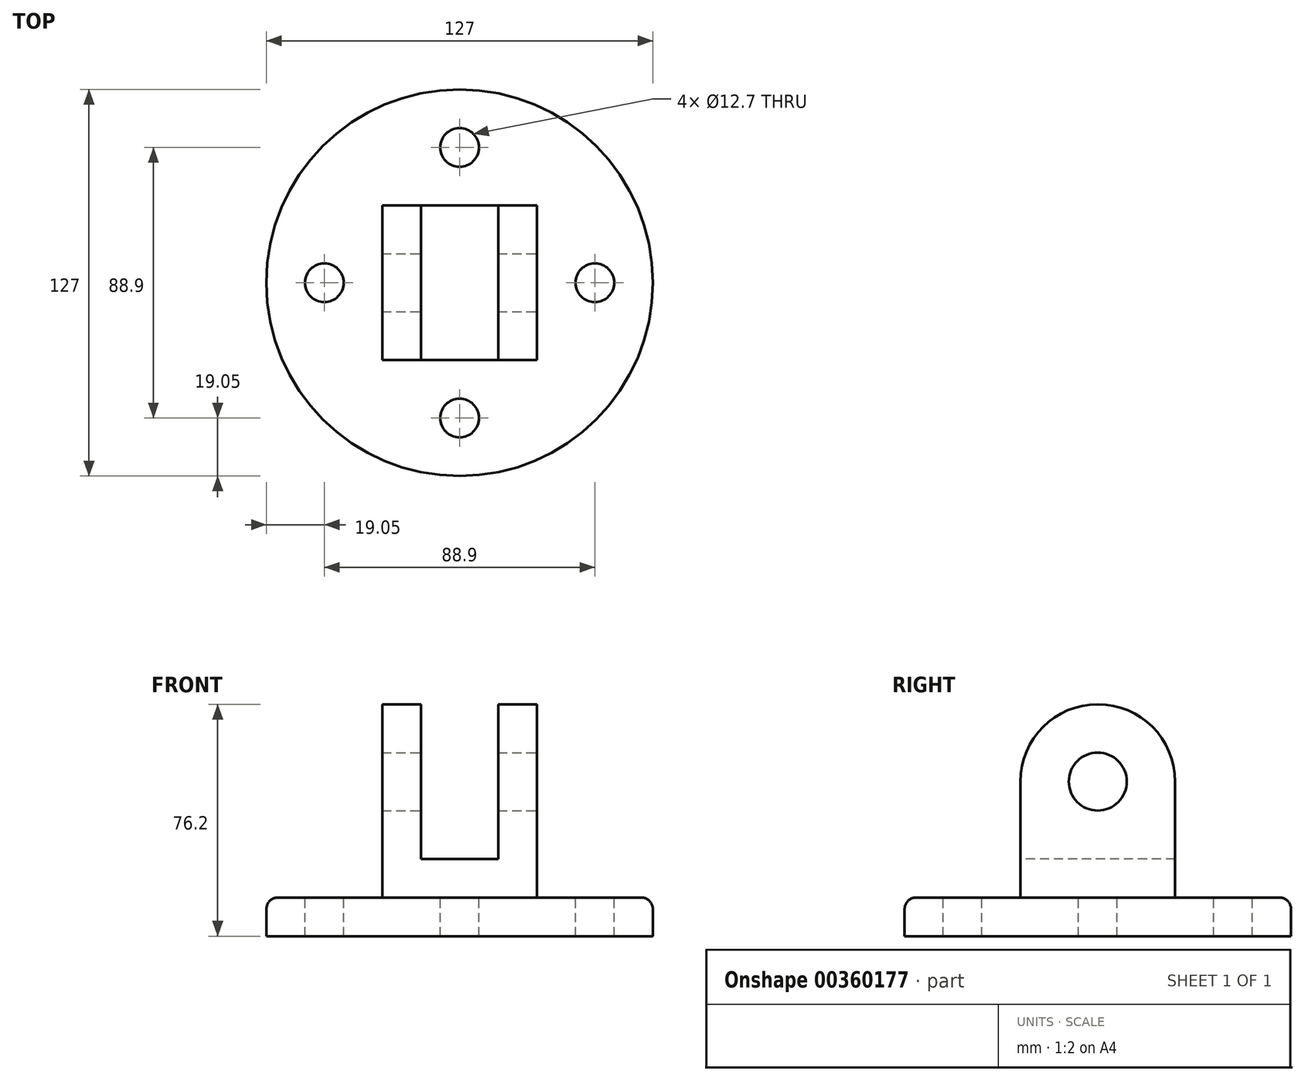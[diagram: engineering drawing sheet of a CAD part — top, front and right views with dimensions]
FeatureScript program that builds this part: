
annotation { "Feature Type Name" : "Feature", "Feature Type Description" : "" }
export const myFeature = defineFeature(function(context is Context, id is Id, definition is map)
    precondition{}
    {
        {
            var Q0;
            Q0=qCreatedBy(makeId("Top.planeOp"),FACE);
            var sketch = newSketch(context, id + "F0", { "sketchPlane" : qUnion([Q0])});
            skCircle(sketch, "E0", {"center": v(0, 0) * mm, "radius": 63.5 * mm});
            skSolve(sketch);
        }
        {
            var Q0;
            Q0=makeQuery(id+"F0.imprint","IMPRINT",FACE,{"disambiguationData":[TD([[makeQuery(id+"F0.imprint","IMPRINT",EDGE,{"derivedFrom":sQuery(id+"F0.wireOp",EDGE,"E0")}),1.0]])]});
            extrude(context, id + "F1", {"entities" : qUnion([Q0]), "depth" : 12.7 * mm});
        }
        {
            var Q0;
            Q0=makeQuery(id+"F1.opExtrude","CAP_FACE",FACE,{"disambiguationData":[OSD([sQuery(id+"F0.wireOp",EDGE,"E0")])],"isStart":false});
            var sketch = newSketch(context, id + "F2", { "sketchPlane" : qUnion([Q0])});
            skCircle(sketch, "E1", {"center": v(0, 0) * mm, "radius": 44.45 * mm, "construction": true});
            skPoint(sketch, "E2", {"position": v(0, 44.45) * mm});
            skPoint(sketch, "E3", {"position": v(-44.45, 0) * mm});
            skPoint(sketch, "E4", {"position": v(0, -44.45) * mm});
            skPoint(sketch, "E5", {"position": v(44.45, 0) * mm});
            skSolve(sketch);
        }
        {
            var Q0;
            Q0=sQuery(id+"F2.wireOp",VERTEX,"E2");
            var Q1;
            Q1=sQuery(id+"F2.wireOp",VERTEX,"E3");
            var Q2;
            Q2=sQuery(id+"F2.wireOp",VERTEX,"E4");
            var Q3;
            Q3=sQuery(id+"F2.wireOp",VERTEX,"E5");
            var Q4;
            Q4=makeQuery(id+"F1.opExtrude","SWEPT_BODY",BODY,{"disambiguationData":[OSD([sQuery(id+"F0.wireOp",EDGE,"E0")])]});
            hole(context, id + "F3", {"style" : HoleStyle.SIMPLE, "endStyle" : HoleEndStyle.THROUGH, "holeDiameter" : 12.7 * mm, "isTappedThrough" : true, "tappedDepth" : 12.7 * mm, "tapClearance" : 3, "locations" : qUnion([Q0, Q1, Q2, Q3]), "scope" : qUnion([Q4])});
        }
        {
            var Q0;
            Q0=qCreatedBy(makeId("Front.planeOp"),FACE);
            var sketch = newSketch(context, id + "F4", { "sketchPlane" : qUnion([Q0])});
            skLineSegment(sketch, "E6.top", {"start": v(-25.4, 50.8) * mm, "end": v(25.4, 50.8) * mm});
            skLineSegment(sketch, "E6.left", {"start": v(-25.4, 12.7) * mm, "end": v(-25.4, 50.8) * mm});
            skLineSegment(sketch, "E6.right", {"start": v(25.4, 12.7) * mm, "end": v(25.4, 50.8) * mm});
            skLineSegment(sketch, "E7", {"start": v(25.4, 12.7) * mm, "end": v(-25.4, 12.7) * mm});
            skSolve(sketch);
        }
        {
            var Q0;
            Q0=makeQuery(id+"F4.imprint","IMPRINT",FACE,{"disambiguationData":[TD([[makeQuery(id+"F4.imprint","IMPRINT",EDGE,{"derivedFrom":sQuery(id+"F4.wireOp",EDGE,"E6.top")}),-1.0]])]});
            extrude(context, id + "F5", {"entities" : qUnion([Q0]), "operationType" : NewBodyOperationType.ADD, "endBound" : BoundingType.SYMMETRIC, "depth" : 50.8 * mm});
        }
        {
            var Q0;
            Q0=makeQuery(id+"F5.opExtrude","CAP_FACE",FACE,{"disambiguationData":[OSD([sQuery(id+"F4.wireOp",EDGE,"E6.top"),sQuery(id+"F4.wireOp",EDGE,"E6.left"),sQuery(id+"F4.wireOp",EDGE,"E6.right"),sQuery(id+"F4.wireOp",EDGE,"E7")])],"isStart":false});
            var sketch = newSketch(context, id + "F6", { "sketchPlane" : qUnion([Q0])});
            skLineSegment(sketch, "E8.bottom", {"start": v(-12.7, 50.8) * mm, "end": v(12.7, 50.8) * mm});
            skLineSegment(sketch, "E8.top", {"start": v(-12.7, 25.4) * mm, "end": v(12.7, 25.4) * mm});
            skLineSegment(sketch, "E8.left", {"start": v(-12.7, 50.8) * mm, "end": v(-12.7, 25.4) * mm});
            skLineSegment(sketch, "E8.right", {"start": v(12.7, 50.8) * mm, "end": v(12.7, 25.4) * mm});
            skSolve(sketch);
        }
        {
            var Q0;
            Q0=makeQuery(id+"F6.imprint","IMPRINT",FACE,{"disambiguationData":[TD([[makeQuery(id+"F6.imprint","IMPRINT",EDGE,{"derivedFrom":sQuery(id+"F6.wireOp",EDGE,"E8.bottom")}),-1.0]])]});
            extrude(context, id + "F7", {"entities" : qUnion([Q0]), "operationType" : NewBodyOperationType.REMOVE, "endBound" : BoundingType.THROUGH_ALL, "oppositeDirection" : true, "depth" : 25.4 * mm});
        }
        {
            var Q0;
            Q0=makeQuery(id+"F1.opExtrude","CAP_EDGE",EDGE,{"disambiguationData":[OSD([sQuery(id+"F0.wireOp",EDGE,"E0")])],"isStart":false});
            var Q1;
            Q1=makeQuery(id+"F5.opExtrude","CAP_EDGE",EDGE,{"disambiguationData":[OSD([sQuery(id+"F4.wireOp",EDGE,"E7")])],"isStart":false});
            var Q2;
            Q2=makeQuery(id+"F5.opExtrude","SWEPT_EDGE",EDGE,{"disambiguationData":[OSD([sQuery(id+"F4.wireOp",EDGE,"E6.right"),sQuery(id+"F4.wireOp",EDGE,"E7")])]});
            var Q3;
            Q3=makeQuery(id+"F5.opExtrude","SWEPT_EDGE",EDGE,{"disambiguationData":[OSD([sQuery(id+"F4.wireOp",EDGE,"E6.left"),sQuery(id+"F4.wireOp",EDGE,"E7")])]});
            var Q4;
            Q4=makeQuery(id+"F5.opExtrude","CAP_EDGE",EDGE,{"disambiguationData":[OSD([sQuery(id+"F4.wireOp",EDGE,"E7")])],"isStart":true});
            fillet(context, id + "F8", {"entities" : qUnion([Q0, Q1, Q2, Q3, Q4]), "radius" : 3.8 * mm, "tangentPropagation" : true, "allowEdgeOverflow" : false});
        }
        {
            var Q0;
            Q0=makeQuery(id+"F5.opExtrude","SWEPT_FACE",FACE,{"disambiguationData":[OSD([sQuery(id+"F4.wireOp",EDGE,"E6.left")])]});
            var sketch = newSketch(context, id + "F9", { "sketchPlane" : qUnion([Q0])});
            skArc(sketch, "E9", {"start": v(25.4, 50.8) * mm, "mid": v(0, 76.2) * mm, "end": v(-25.4, 50.8) * mm});
            skSolve(sketch);
        }
        {
            var Q0;
            Q0=makeQuery(id+"F5.opExtrude","SWEPT_FACE",FACE,{"disambiguationData":[OSD([sQuery(id+"F4.wireOp",EDGE,"E6.right")])]});
            var sketch = newSketch(context, id + "F10", { "sketchPlane" : qUnion([Q0])});
            skArc(sketch, "E10", {"start": v(25.4, 50.8) * mm, "mid": v(0, 76.2) * mm, "end": v(-25.4, 50.8) * mm});
            skSolve(sketch);
        }
        {
            var Q0;
            Q0=makeQuery(id+"F9.imprint","IMPRINT",FACE,{"disambiguationData":[TD([[makeQuery(id+"F9.imprint","IMPRINT",EDGE,{"derivedFrom":sQuery(id+"F9.wireOp",EDGE,"E9")}),1.0]])]});
            extrude(context, id + "F11", {"entities" : qUnion([Q0]), "operationType" : NewBodyOperationType.ADD, "oppositeDirection" : true, "depth" : 12.7 * mm});
        }
        {
            var Q0;
            Q0=makeQuery(id+"F10.imprint","IMPRINT",FACE,{"disambiguationData":[TD([[makeQuery(id+"F10.imprint","IMPRINT",EDGE,{"derivedFrom":sQuery(id+"F10.wireOp",EDGE,"E10")}),1.0]])]});
            extrude(context, id + "F12", {"entities" : qUnion([Q0]), "operationType" : NewBodyOperationType.ADD, "oppositeDirection" : true, "depth" : 12.7 * mm});
        }
        {
            var Q0;
            {var subQ0=sQuery(id+"F4.wireOp",EDGE,"E6.right");Q0=makeQuery(id+"F12.boolean.opBoolean","MERGE",FACE,{"derivedFrom":[makeQuery(id+"F5.opExtrude","SWEPT_FACE",FACE,{"disambiguationData":[OSD([subQ0])]}),makeQuery(id+"F12.opExtrude","CAP_FACE",FACE,{"disambiguationData":[OSD([sQuery(id+"F4.wireOp",EDGE,"E6.top"),subQ0,sQuery(id+"F10.wireOp",EDGE,"E10")])],"isStart":true})]});}
            var sketch = newSketch(context, id + "F13", { "sketchPlane" : qUnion([Q0])});
            skCircle(sketch, "E11", {"center": v(0, 50.8) * mm, "radius": 9.53 * mm});
            skSolve(sketch);
        }
        {
            var Q0;
            Q0=makeQuery(id+"F13.imprint","IMPRINT",FACE,{"disambiguationData":[TD([[makeQuery(id+"F13.imprint","IMPRINT",EDGE,{"derivedFrom":sQuery(id+"F13.wireOp",EDGE,"E11")}),1.0]])]});
            extrude(context, id + "F14", {"entities" : qUnion([Q0]), "operationType" : NewBodyOperationType.REMOVE, "endBound" : BoundingType.THROUGH_ALL, "oppositeDirection" : true, "depth" : 25.4 * mm});
        }
    });
